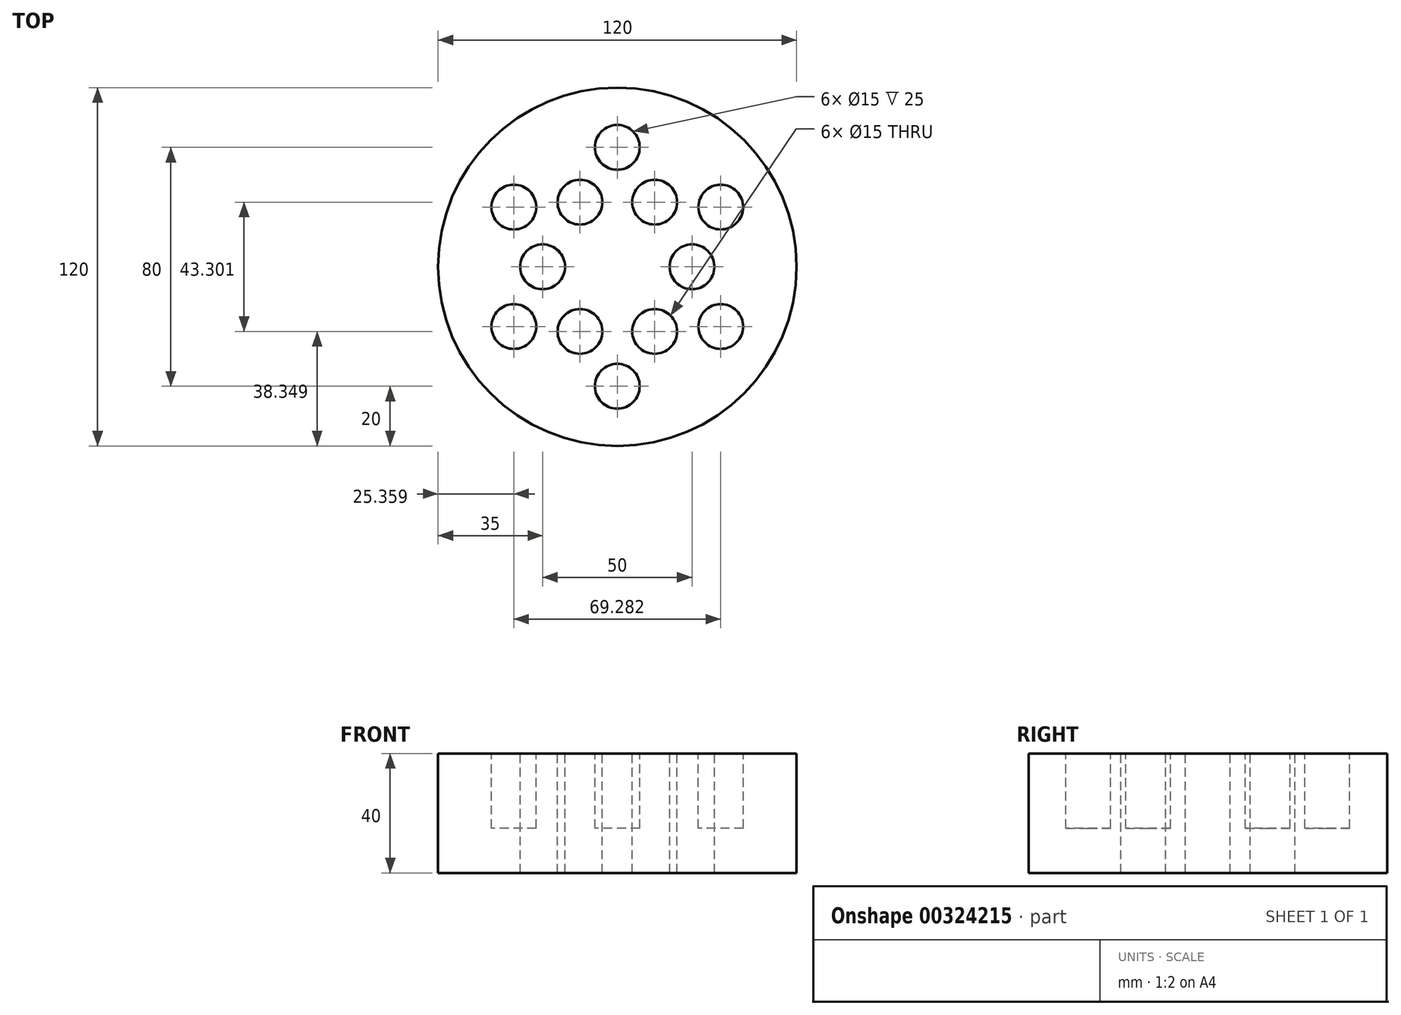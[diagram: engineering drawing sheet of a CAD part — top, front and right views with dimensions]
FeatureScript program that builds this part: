
annotation { "Feature Type Name" : "Feature", "Feature Type Description" : "" }
export const myFeature = defineFeature(function(context is Context, id is Id, definition is map)
    precondition{}
    {
        {
            var Q0;
            Q0=qCreatedBy(makeId("Top.planeOp"),FACE);
            var sketch = newSketch(context, id + "F0", { "sketchPlane" : qUnion([Q0])});
            skCircle(sketch, "E0", {"center": v(0, 0) * mm, "radius": 60 * mm});
            skSolve(sketch);
        }
        {
            var Q0;
            Q0=makeQuery(id+"F0.imprint","IMPRINT",FACE,{"disambiguationData":[TD([[makeQuery(id+"F0.imprint","IMPRINT",EDGE,{"derivedFrom":sQuery(id+"F0.wireOp",EDGE,"E0")}),1.0]])]});
            extrude(context, id + "F1", {"entities" : qUnion([Q0]), "depth" : 40 * mm});
        }
        {
            var Q0;
            Q0=makeQuery(id+"F1.opExtrude","CAP_FACE",FACE,{"disambiguationData":[OSD([sQuery(id+"F0.wireOp",EDGE,"E0")])],"isStart":false});
            var sketch = newSketch(context, id + "F2", { "sketchPlane" : qUnion([Q0])});
            skCircle(sketch, "E1", {"center": v(0, 40) * mm, "radius": 7.5 * mm});
            skCircle(sketch, "E2.1.0", {"center": v(-34.64, 20) * mm, "radius": 7.5 * mm});
            skCircle(sketch, "E2.2.0", {"center": v(-34.64, -20) * mm, "radius": 7.5 * mm});
            skCircle(sketch, "E2.3.0", {"center": v(0, -40) * mm, "radius": 7.5 * mm});
            skCircle(sketch, "E2.4.0", {"center": v(34.64, -20) * mm, "radius": 7.5 * mm});
            skCircle(sketch, "E2.5.0", {"center": v(34.64, 20) * mm, "radius": 7.5 * mm});
            skPoint(sketch, "E2.center", {"position": v(0, 0) * mm});
            skSolve(sketch);
        }
        {
            var Q0;
            Q0=makeQuery(id+"F2.imprint","IMPRINT",FACE,{"disambiguationData":[TD([[makeQuery(id+"F2.imprint","IMPRINT",EDGE,{"derivedFrom":sQuery(id+"F2.wireOp",EDGE,"E2.1.0")}),1.0]])]});
            var Q1;
            Q1=makeQuery(id+"F2.imprint","IMPRINT",FACE,{"disambiguationData":[TD([[makeQuery(id+"F2.imprint","IMPRINT",EDGE,{"derivedFrom":sQuery(id+"F2.wireOp",EDGE,"E1")}),1.0]])]});
            var Q2;
            Q2=makeQuery(id+"F2.imprint","IMPRINT",FACE,{"disambiguationData":[TD([[makeQuery(id+"F2.imprint","IMPRINT",EDGE,{"derivedFrom":sQuery(id+"F2.wireOp",EDGE,"E2.7.0")}),1.0]])]});
            var Q3;
            Q3=makeQuery(id+"F2.imprint","IMPRINT",FACE,{"disambiguationData":[TD([[makeQuery(id+"F2.imprint","IMPRINT",EDGE,{"derivedFrom":sQuery(id+"F2.wireOp",EDGE,"E2.6.0")}),1.0]])]});
            var Q4;
            Q4=makeQuery(id+"F2.imprint","IMPRINT",FACE,{"disambiguationData":[TD([[makeQuery(id+"F2.imprint","IMPRINT",EDGE,{"derivedFrom":sQuery(id+"F2.wireOp",EDGE,"E2.5.0")}),1.0]])]});
            var Q5;
            Q5=makeQuery(id+"F2.imprint","IMPRINT",FACE,{"disambiguationData":[TD([[makeQuery(id+"F2.imprint","IMPRINT",EDGE,{"derivedFrom":sQuery(id+"F2.wireOp",EDGE,"E2.4.0")}),1.0]])]});
            var Q6;
            Q6=makeQuery(id+"F2.imprint","IMPRINT",FACE,{"disambiguationData":[TD([[makeQuery(id+"F2.imprint","IMPRINT",EDGE,{"derivedFrom":sQuery(id+"F2.wireOp",EDGE,"E2.3.0")}),1.0]])]});
            var Q7;
            Q7=makeQuery(id+"F2.imprint","IMPRINT",FACE,{"disambiguationData":[TD([[makeQuery(id+"F2.imprint","IMPRINT",EDGE,{"derivedFrom":sQuery(id+"F2.wireOp",EDGE,"E2.2.0")}),1.0]])]});
            extrude(context, id + "F3", {"entities" : qUnion([Q0, Q1, Q2, Q3, Q4, Q5, Q6, Q7]), "operationType" : NewBodyOperationType.REMOVE, "oppositeDirection" : true, "depth" : 25 * mm});
        }
        {
            var Q0;
            Q0=makeQuery(id+"F1.opExtrude","CAP_FACE",FACE,{"disambiguationData":[OSD([sQuery(id+"F0.wireOp",EDGE,"E0")])],"isStart":false});
            var sketch = newSketch(context, id + "F4", { "sketchPlane" : qUnion([Q0])});
            skCircle(sketch, "E3", {"center": v(-12.5, 21.65) * mm, "radius": 7.5 * mm});
            skLineSegment(sketch, "E4", {"start": v(0, 0) * mm, "end": v(-12.5, 21.65) * mm});
            skCircle(sketch, "E5.1.0", {"center": v(-25, 0) * mm, "radius": 7.5 * mm});
            skCircle(sketch, "E5.2.0", {"center": v(-12.5, -21.65) * mm, "radius": 7.5 * mm});
            skCircle(sketch, "E5.3.0", {"center": v(12.5, -21.65) * mm, "radius": 7.5 * mm});
            skCircle(sketch, "E5.4.0", {"center": v(25, 0) * mm, "radius": 7.5 * mm});
            skCircle(sketch, "E5.5.0", {"center": v(12.5, 21.65) * mm, "radius": 7.5 * mm});
            skPoint(sketch, "E5.center", {"position": v(0, 0) * mm});
            skSolve(sketch);
        }
        {
            var Q0;
            Q0=makeQuery(id+"F4.imprint","IMPRINT",FACE,{"disambiguationData":[TD([[makeQuery(id+"F4.imprint","IMPRINT",EDGE,{"derivedFrom":sQuery(id+"F4.wireOp",EDGE,"E5.1.0")}),1.0]])]});
            var Q1;
            Q1=makeQuery(id+"F4.imprint","IMPRINT",FACE,{"disambiguationData":[TD([[makeQuery(id+"F4.imprint","IMPRINT",EDGE,{"derivedFrom":sQuery(id+"F4.wireOp",EDGE,"E5.2.0")}),1.0]])]});
            var Q2;
            Q2=makeQuery(id+"F4.imprint","IMPRINT",FACE,{"disambiguationData":[TD([[makeQuery(id+"F4.imprint","IMPRINT",EDGE,{"derivedFrom":sQuery(id+"F4.wireOp",EDGE,"E5.3.0")}),1.0]])]});
            var Q3;
            Q3=makeQuery(id+"F4.imprint","IMPRINT",FACE,{"disambiguationData":[TD([[makeQuery(id+"F4.imprint","IMPRINT",EDGE,{"derivedFrom":sQuery(id+"F4.wireOp",EDGE,"E5.4.0")}),1.0]])]});
            var Q4;
            Q4=makeQuery(id+"F4.imprint","IMPRINT",FACE,{"disambiguationData":[TD([[makeQuery(id+"F4.imprint","IMPRINT",EDGE,{"derivedFrom":sQuery(id+"F4.wireOp",EDGE,"E5.5.0")}),1.0]])]});
            var Q5;
            Q5=makeQuery(id+"F4.imprint","IMPRINT",FACE,{"disambiguationData":[TD([[makeQuery(id+"F4.imprint","IMPRINT",EDGE,{"derivedFrom":sQuery(id+"F4.wireOp",EDGE,"E3")}),1.0]])]});
            extrude(context, id + "F5", {"entities" : qUnion([Q0, Q1, Q2, Q3, Q4, Q5]), "operationType" : NewBodyOperationType.REMOVE, "endBound" : BoundingType.THROUGH_ALL, "oppositeDirection" : true, "depth" : 25 * mm});
        }
    });
